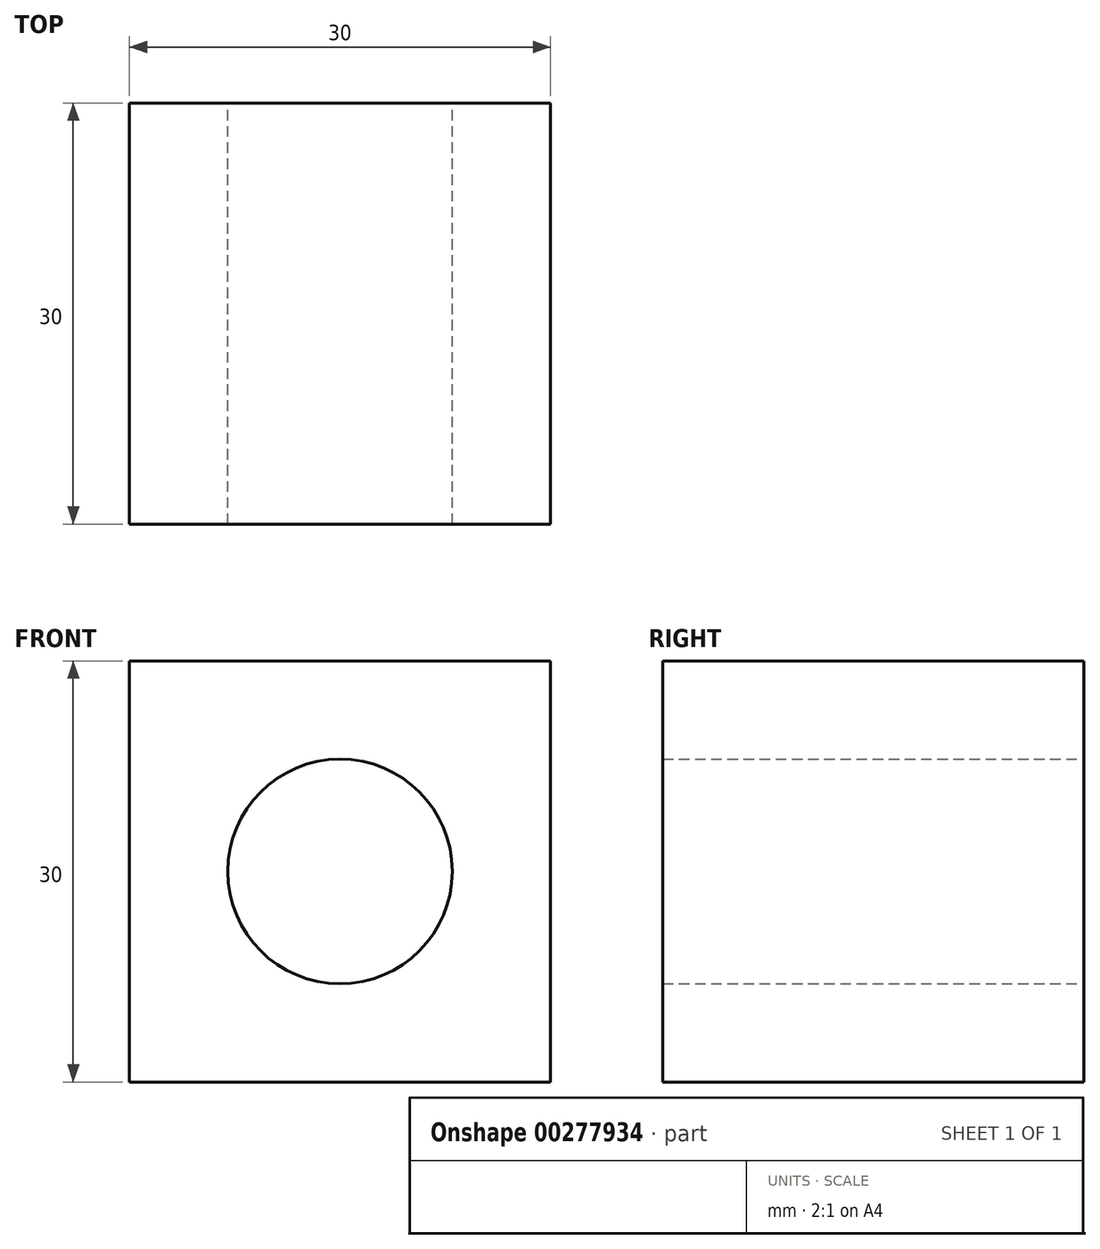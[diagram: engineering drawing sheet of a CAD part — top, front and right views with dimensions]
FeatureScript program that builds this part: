
annotation { "Feature Type Name" : "Feature", "Feature Type Description" : "" }
export const myFeature = defineFeature(function(context is Context, id is Id, definition is map)
    precondition{}
    {
        {
            var Q0;
            Q0=qCreatedBy(makeId("Front.planeOp"),FACE);
            var sketch = newSketch(context, id + "F0", { "sketchPlane" : qUnion([Q0])});
            skLineSegment(sketch, "E0.bottom", {"start": v(15, -15) * mm, "end": v(-15, -15) * mm});
            skLineSegment(sketch, "E0.top", {"start": v(15, 15) * mm, "end": v(-15, 15) * mm});
            skLineSegment(sketch, "E0.left", {"start": v(15, -15) * mm, "end": v(15, 15) * mm});
            skLineSegment(sketch, "E0.right", {"start": v(-15, -15) * mm, "end": v(-15, 15) * mm});
            skPoint(sketch, "E0.middle", {"position": v(0, 0) * mm});
            skCircle(sketch, "E1", {"center": v(0, 0) * mm, "radius": 8 * mm});
            skSolve(sketch);
        }
        {
            var Q0;
            Q0 = qSketchRegion(id + "F0", true);
            extrude(context, id + "F1", {"entities" : qUnion([Q0]), "depth" : 30 * mm});
        }
    });
